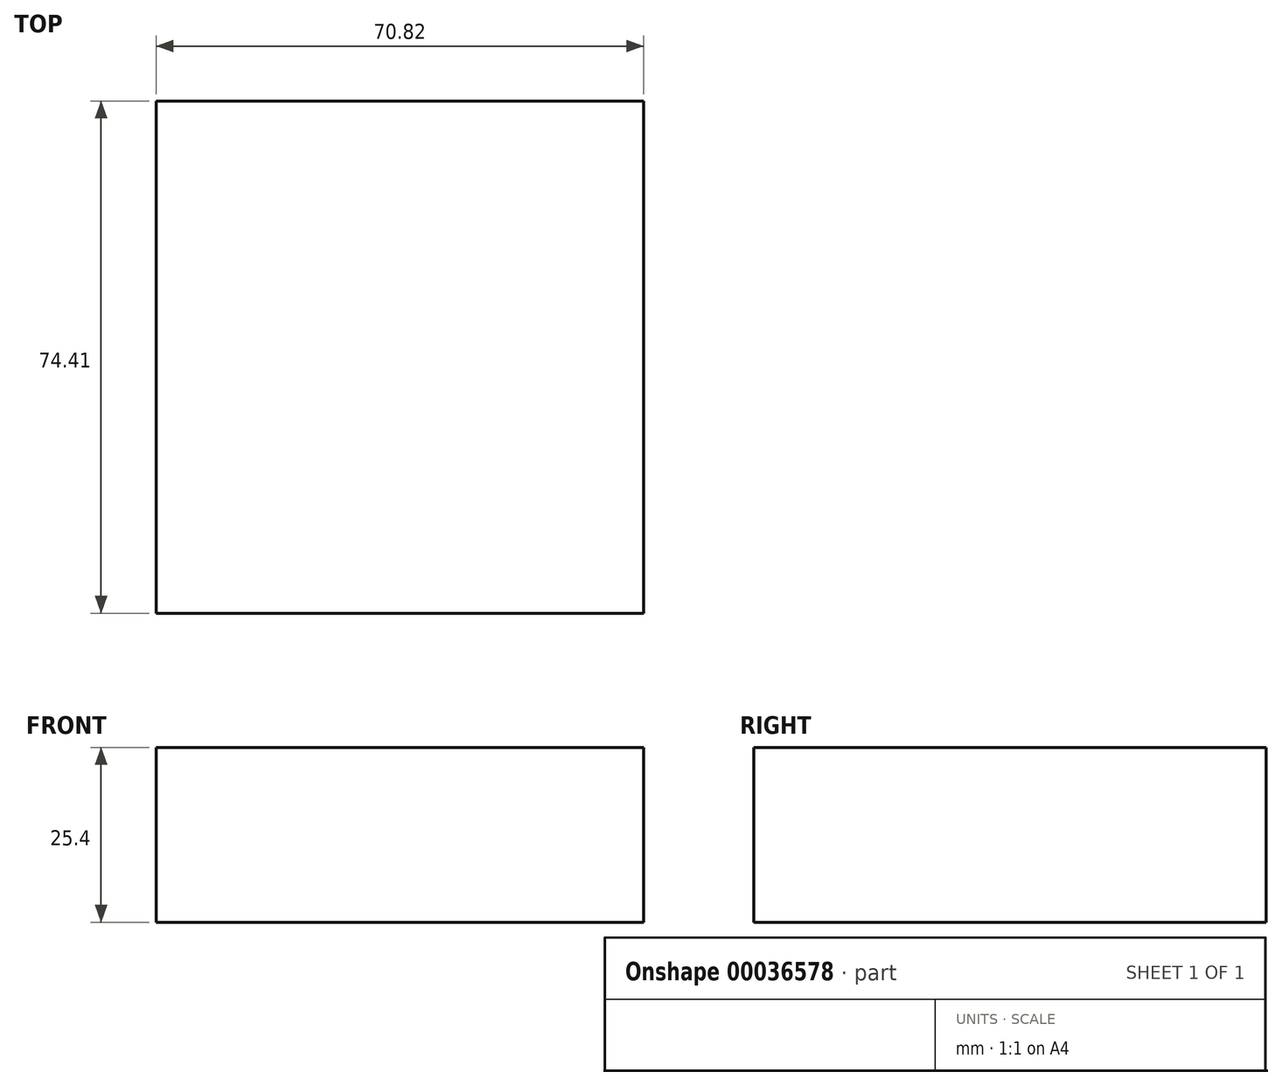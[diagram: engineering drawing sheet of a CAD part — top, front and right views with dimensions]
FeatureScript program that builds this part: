
annotation { "Feature Type Name" : "Feature", "Feature Type Description" : "" }
export const myFeature = defineFeature(function(context is Context, id is Id, definition is map)
    precondition{}
    {
        {
            var Q0;
            Q0=qCreatedBy(makeId("Top.planeOp"),FACE);
            var sketch = newSketch(context, id + "F0", { "sketchPlane" : qUnion([Q0])});
            skLineSegment(sketch, "E0.bottom", {"start": v(-35.37, 40.85) * mm, "end": v(35.45, 40.85) * mm});
            skLineSegment(sketch, "E0.top", {"start": v(-35.37, -33.56) * mm, "end": v(35.45, -33.56) * mm});
            skLineSegment(sketch, "E0.left", {"start": v(-35.37, 40.85) * mm, "end": v(-35.37, -33.56) * mm});
            skLineSegment(sketch, "E0.right", {"start": v(35.45, 40.85) * mm, "end": v(35.45, -33.56) * mm});
            skSolve(sketch);
        }
        {
            var Q0;
            Q0=makeQuery(id+"F0.imprint","IMPRINT",FACE,{"disambiguationData":[TD([[makeQuery(id+"F0.imprint","IMPRINT",EDGE,{"derivedFrom":sQuery(id+"F0.wireOp",EDGE,"E0.bottom")}),-1.0]])]});
            extrude(context, id + "F1", {"entities" : qUnion([Q0]), "depth" : 25.4 * mm});
        }
    });
